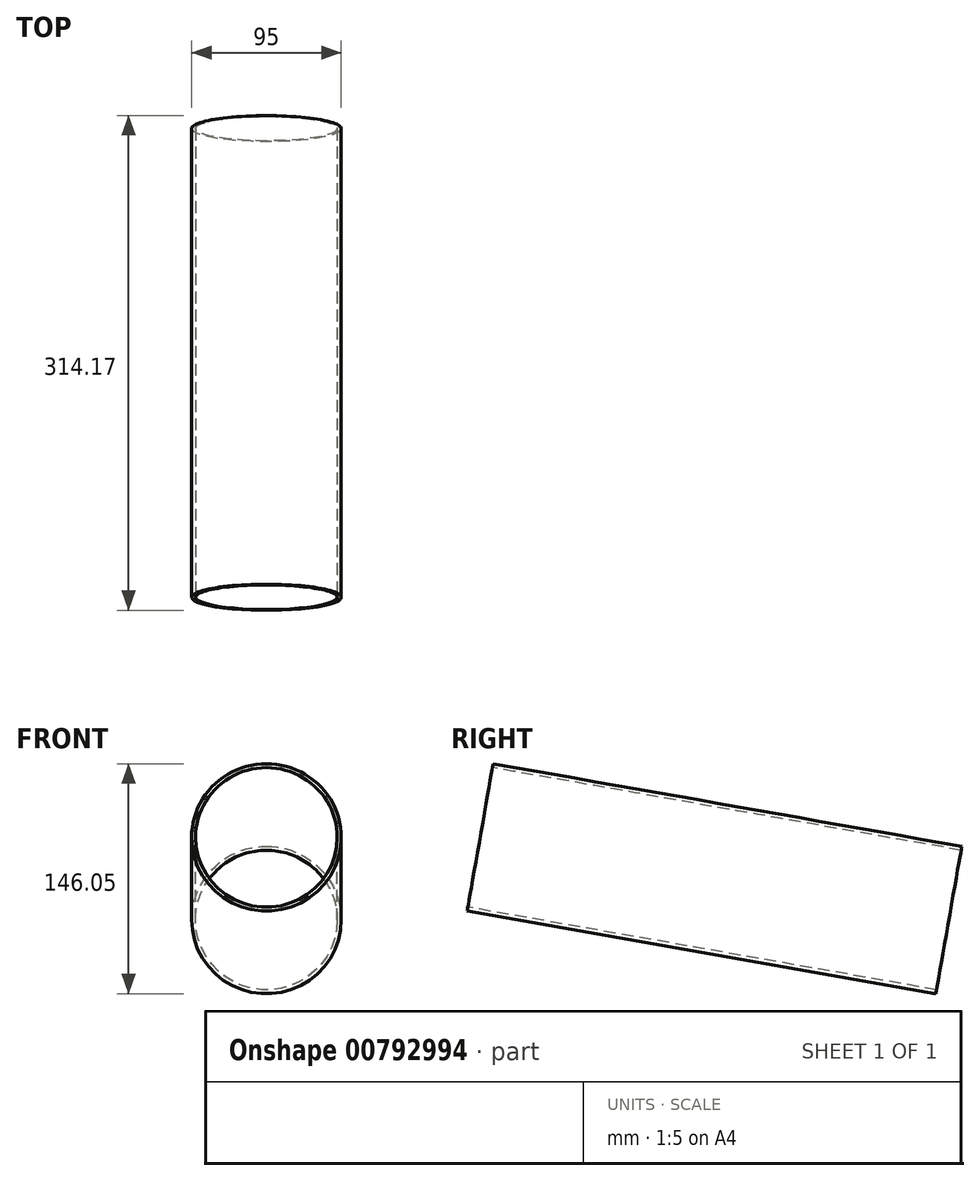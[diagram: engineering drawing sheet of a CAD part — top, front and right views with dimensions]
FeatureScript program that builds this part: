
annotation { "Feature Type Name" : "Feature", "Feature Type Description" : "" }
export const myFeature = defineFeature(function(context is Context, id is Id, definition is map)
    precondition{}
    {
        {
            var Q0;
            Q0=qCreatedBy(makeId("Front.planeOp"),FACE);
            var sketch = newSketch(context, id + "F0", { "sketchPlane" : qUnion([Q0])});
            skLineSegment(sketch, "E0", {"start": v(-72.3, 0) * mm, "end": v(82, 0) * mm});
            skSolve(sketch);
        }
        {
            var Q0;
            Q0=sQuery(id+"F0.wireOp",EDGE,"E0");
            var Q1;
            Q1=qCreatedBy(makeId("Front.planeOp"),FACE);
            cPlane(context, id + "F1", {"entities" : qUnion([Q0, Q1]), "cplaneType" : CPlaneType.LINE_ANGLE, "offset" : 25.4 * mm, "angle" : 10 * degree, "oppositeDirection" : true, "width" : 152.4 * mm, "height" : 152.4 * mm});
        }
        {
            var Q0;
            Q0=qCreatedBy(id+"F1.planeOp",FACE);
            var sketch = newSketch(context, id + "F2", { "sketchPlane" : qUnion([Q0])});
            skCircle(sketch, "E1", {"center": v(0, 0) * mm, "radius": 47.5 * mm});
            skSolve(sketch);
        }
        {
            var Q0;
            Q0 = qSketchRegion(id + "F2", true);
            extrude(context, id + "F3", {"entities" : qUnion([Q0]), "depth" : 302.26 * mm, "offsetDistance" : 25.4 * mm});
        }
        {
            var Q0;
            Q0=makeQuery(id+"F3.opExtrude","CAP_FACE",FACE,{"disambiguationData":[OSD([sQuery(id+"F2.wireOp",EDGE,"E1")])],"isStart":true});
            var Q1;
            Q1=makeQuery(id+"F3.opExtrude","CAP_FACE",FACE,{"disambiguationData":[OSD([sQuery(id+"F2.wireOp",EDGE,"E1")])],"isStart":false});
            shell(context, id + "F4", {"entities" : qUnion([Q0, Q1]), "thickness" : 2.5 * mm});
        }
    });
